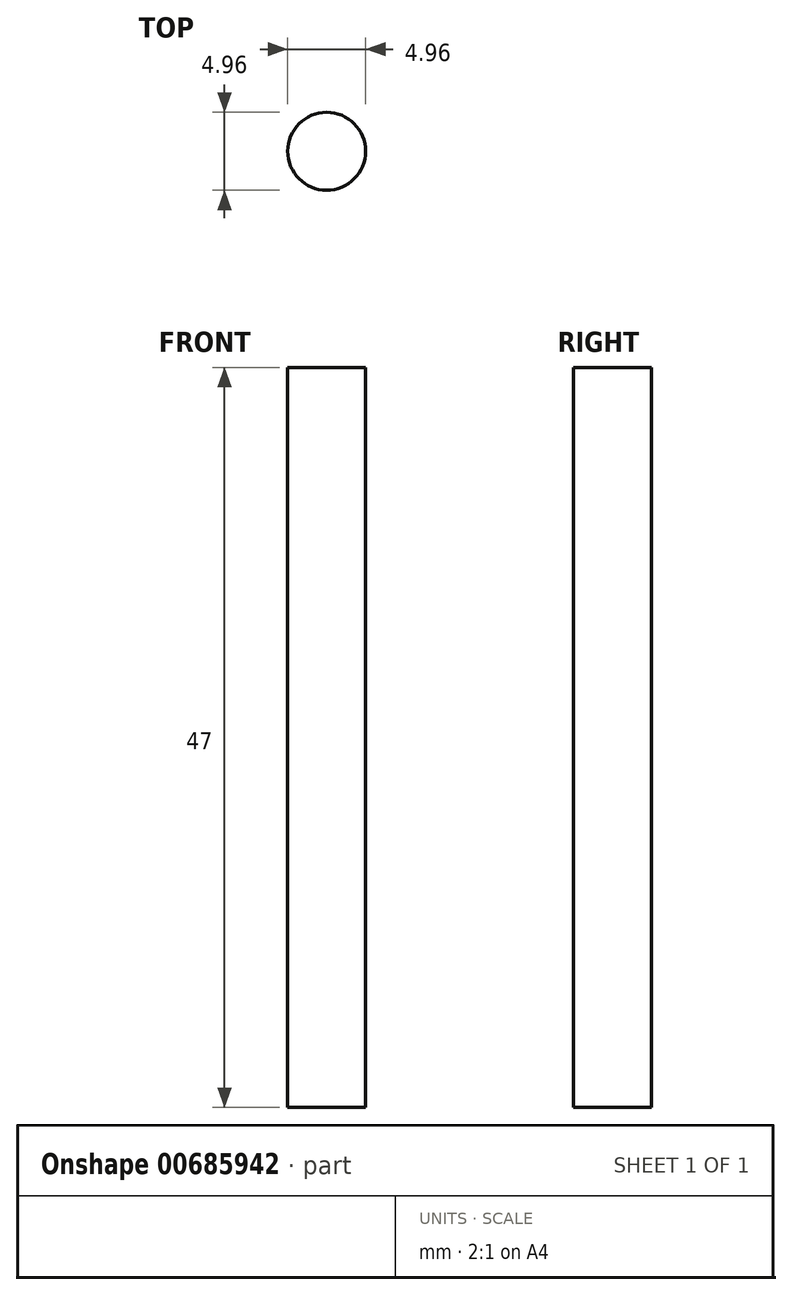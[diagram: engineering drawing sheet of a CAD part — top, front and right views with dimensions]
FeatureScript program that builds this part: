
annotation { "Feature Type Name" : "Feature", "Feature Type Description" : "" }
export const myFeature = defineFeature(function(context is Context, id is Id, definition is map)
    precondition{}
    {
        {
            var Q0;
            Q0=qCreatedBy(makeId("Top.planeOp"),FACE);
            var sketch = newSketch(context, id + "F0", { "sketchPlane" : qUnion([Q0])});
            skCircle(sketch, "E0", {"center": v(0, 0) * mm, "radius": 2.48 * mm});
            skSolve(sketch);
        }
        {
            var Q0;
            Q0=makeQuery(id+"F0.imprint","IMPRINT",FACE,{"disambiguationData":[TD([[makeQuery(id+"F0.imprint","IMPRINT",EDGE,{"derivedFrom":sQuery(id+"F0.wireOp",EDGE,"E0")}),1.0]])]});
            extrude(context, id + "F1", {"entities" : qUnion([Q0]), "depth" : 47 * mm, "offsetDistance" : 25 * mm});
        }
    });
